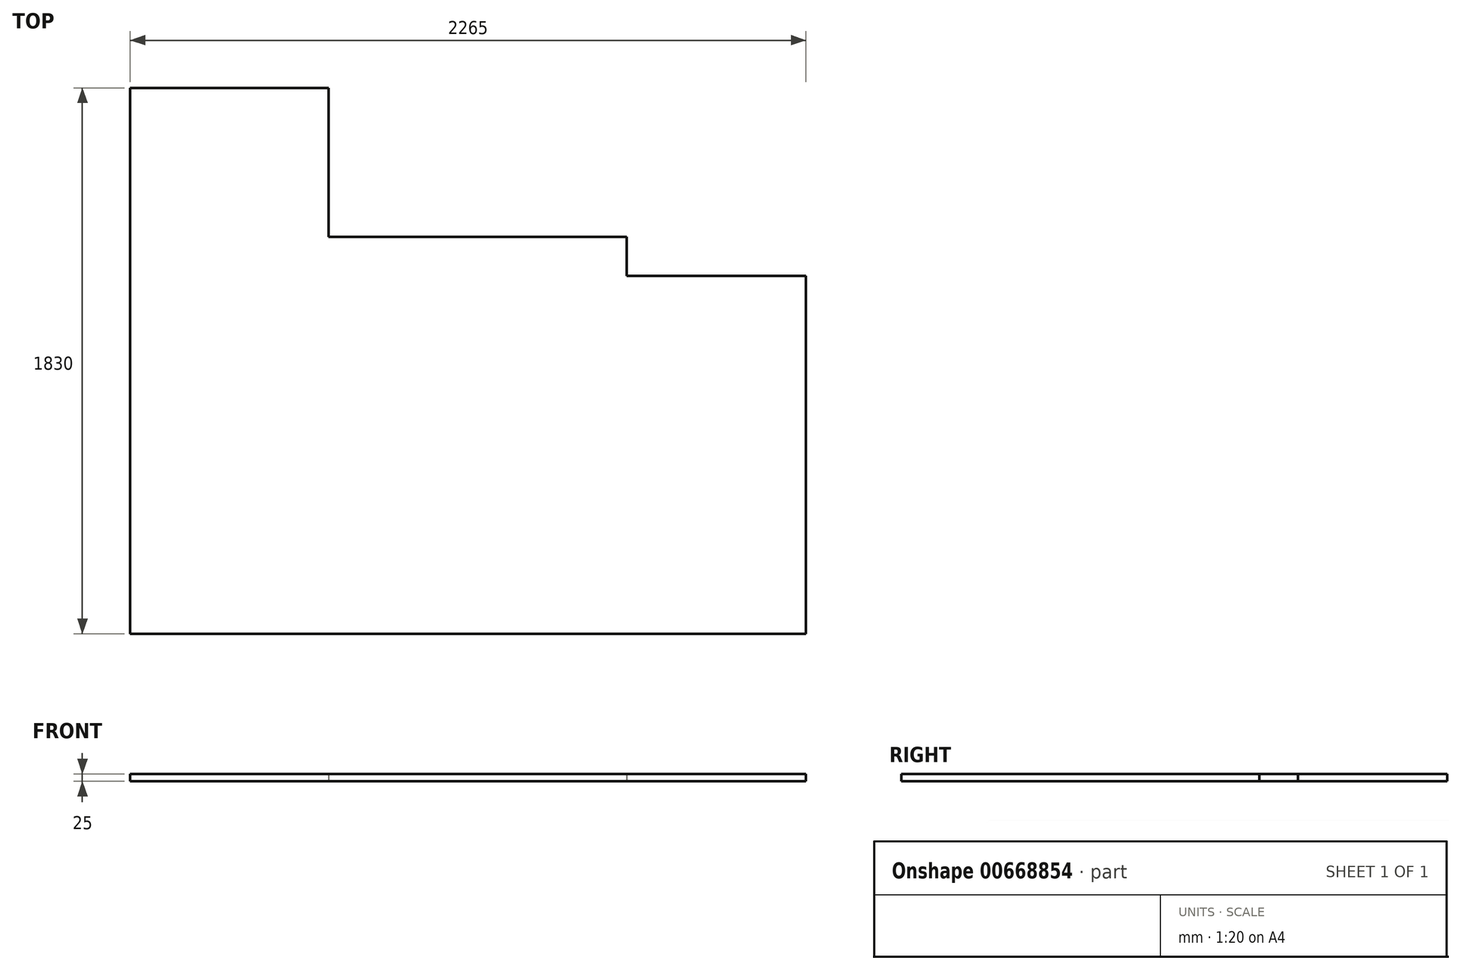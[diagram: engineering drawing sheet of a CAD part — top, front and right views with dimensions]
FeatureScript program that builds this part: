
annotation { "Feature Type Name" : "Feature", "Feature Type Description" : "" }
export const myFeature = defineFeature(function(context is Context, id is Id, definition is map)
    precondition{}
    {
        {
            var Q0;
            Q0=qCreatedBy(makeId("Top.planeOp"),FACE);
            var sketch = newSketch(context, id + "F0", { "sketchPlane" : qUnion([Q0])});
            skLineSegment(sketch, "E0.bottom", {"start": v(-1132.5, -915) * mm, "end": v(1132.5, -915) * mm});
            skLineSegment(sketch, "E0.top", {"start": v(-1132.5, 915) * mm, "end": v(1132.5, 915) * mm});
            skLineSegment(sketch, "E0.left", {"start": v(-1132.5, -915) * mm, "end": v(-1132.5, 915) * mm});
            skLineSegment(sketch, "E0.right", {"start": v(1132.5, -915) * mm, "end": v(1132.5, 915) * mm});
            skPoint(sketch, "E0.middle", {"position": v(0, 0) * mm});
            skLineSegment(sketch, "E1.bottom", {"start": v(1132.5, 915) * mm, "end": v(532.5, 915) * mm});
            skLineSegment(sketch, "E1.top", {"start": v(1132.5, 285) * mm, "end": v(532.5, 285) * mm});
            skLineSegment(sketch, "E1.left", {"start": v(1132.5, 915) * mm, "end": v(1132.5, 285) * mm});
            skLineSegment(sketch, "E1.right", {"start": v(532.5, 915) * mm, "end": v(532.5, 285) * mm});
            skLineSegment(sketch, "E2.bottom", {"start": v(532.5, 915) * mm, "end": v(-467.5, 915) * mm});
            skLineSegment(sketch, "E2.top", {"start": v(532.5, 415) * mm, "end": v(-467.5, 415) * mm});
            skLineSegment(sketch, "E2.left", {"start": v(532.5, 915) * mm, "end": v(532.5, 415) * mm});
            skLineSegment(sketch, "E2.right", {"start": v(-467.5, 915) * mm, "end": v(-467.5, 415) * mm});
            skSolve(sketch);
        }
        {
            var Q0;
            Q0=makeQuery(id+"F0.imprint","IMPRINT",FACE,{"disambiguationData":[TD([[makeQuery(id+"F0.imprint","IMPRINT",EDGE,{"derivedFrom":sQuery(id+"F0.wireOp",EDGE,"E0.bottom")}),1.0]])]});
            extrude(context, id + "F1", {"entities" : qUnion([Q0]), "depth" : 25 * mm, "offsetDistance" : 25 * mm});
        }
    });
